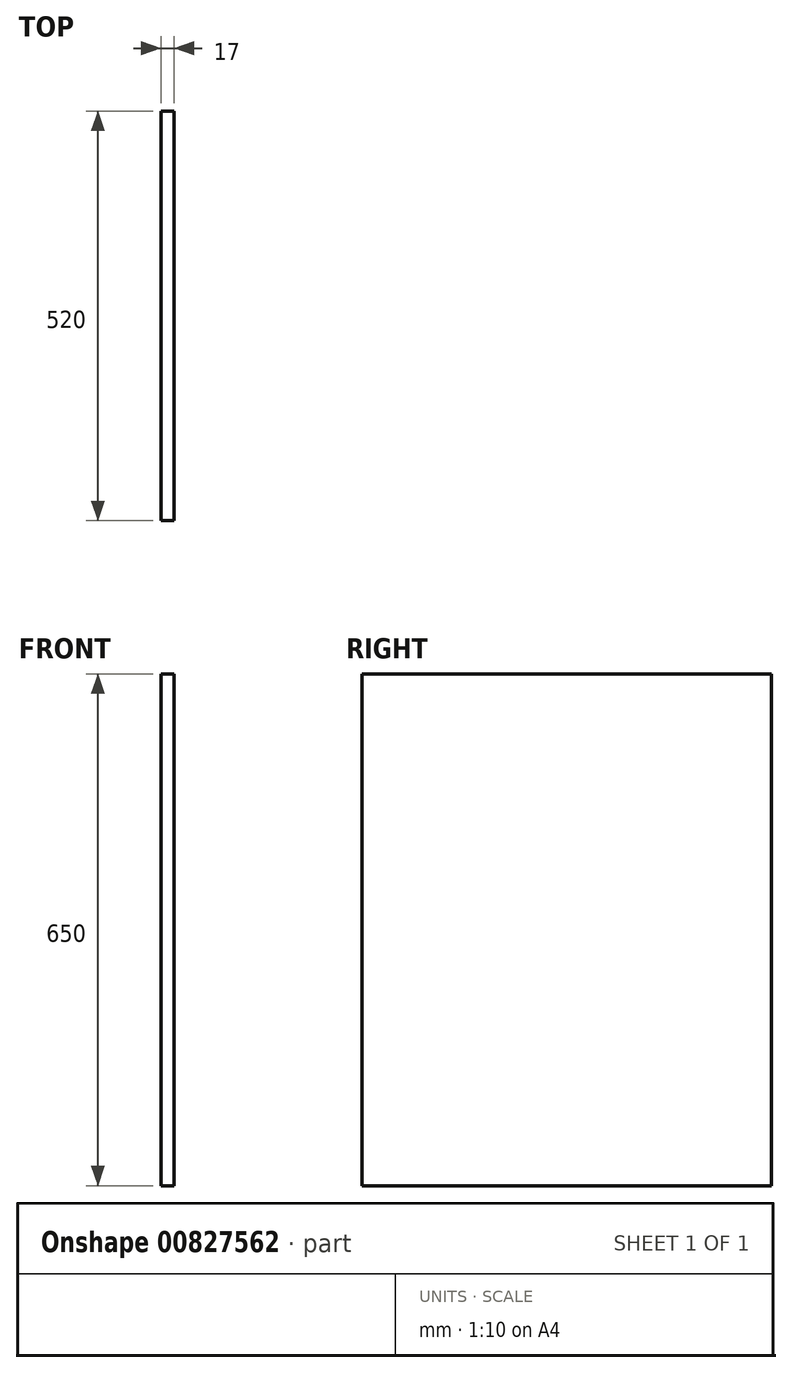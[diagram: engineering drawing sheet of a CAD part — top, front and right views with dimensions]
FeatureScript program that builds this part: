
annotation { "Feature Type Name" : "Feature", "Feature Type Description" : "" }
export const myFeature = defineFeature(function(context is Context, id is Id, definition is map)
    precondition{}
    {
        {
            var Q0;
            Q0=qCreatedBy(makeId("Right.planeOp"),FACE);
            var sketch = newSketch(context, id + "F0", { "sketchPlane" : qUnion([Q0])});
            skLineSegment(sketch, "E0.bottom", {"start": v(0, 0) * mm, "end": v(-520, 0) * mm});
            skLineSegment(sketch, "E0.top", {"start": v(0, 650) * mm, "end": v(-520, 650) * mm});
            skLineSegment(sketch, "E0.left", {"start": v(0, 0) * mm, "end": v(0, 650) * mm});
            skLineSegment(sketch, "E0.right", {"start": v(-520, 0) * mm, "end": v(-520, 650) * mm});
            skSolve(sketch);
        }
        {
            var Q0;
            Q0=makeQuery(id+"F0.imprint","IMPRINT",FACE,{"disambiguationData":[TD([[makeQuery(id+"F0.imprint","IMPRINT",EDGE,{"derivedFrom":sQuery(id+"F0.wireOp",EDGE,"E0.bottom")}),-1.0]])]});
            extrude(context, id + "F1", {"entities" : qUnion([Q0]), "oppositeDirection" : true, "depth" : 17 * mm, "offsetDistance" : 25 * mm});
        }
    });
